# Revit family: LSN Configuration-A
name_source: partatom
category: Electrical Equipment
units: mm (PartAtom-declared; Revit-internal decimal feet)

## family parameters
Cut with Voids When Loaded = No
Host = Face
OmniClass Number = 23.80.30.11.14
OmniClass Title = Inverters
Part Type = Other Panel
Room Calculation Point = No
Round Connector Dimension = Use Diameter
Shared = No

## types (1)
- LSN
    Assembly Code = D5090200
    Battery Type = Battery Type : G = 20-Year VRLA Lead-Calcium
    Capacity Rating = Capacity Rating : 01 = 1.0KVA
    Connector Description = Electrical Connector
    Default Elevation = 48 "
    Depth = 18.63 "
    Description = Single-Phase Central Lighting Inverters
    Height = 46 "
    Housing Material = Metal - Steel - Gray
    Input Voltage = Input Voltage : 120VAC
    Load Classification = Power
    Manufacturer = Dual-Lite
    Model = LSN - D Series
    Output Voltage = Output Voltage : 120/240VAC
    Temperature Range = 20°C - 30°C (68°F - 86°F)
    URL = https://www.currentlighting.com
    Width = 30 "

## geometry (parser evidence)
native form markers: Sweep x20
no freeform markers — native parametric forms only
